# Revit family: 1SE_Trez_TC_2C_T_2500_With_Ramp
name_source: partatom
category: Specialty Equipment
units: mm (PartAtom-declared; Revit-internal decimal feet)

## family parameters
Always vertical = Yes
Cut with Voids When Loaded = Yes
Part Type = Normal
Room Calculation Point = No
Round Connector Dimension = Use Diameter
Shared = No
Work Plane-Based = No

## types (1)
- Platform-2300x2300mm with Door Height 2500mm
    Cabin = Speciality_Equipment_Trez_Cabin : Cabin
    Cabin or Platform = Speciality_Equipment_Trez_Platform : Platform
    Cabin or Platform Back = Yes
    Clear Depth = 2300 mm
    Clear Width = 2300 mm
    Clearance = 475 mm  [stored 1.5584 ft]
    Description = Trez Compact 2 Cylinders Tower. Goods only lift.
    Door Clear Height = 2500 mm  [stored 8.2021 ft]
    Door Clear Width = 2300 mm
    Headroom = 3100 mm
    Manufacturer = TREZ Ltd.
    Model = TC 2C T 2500
    Platform = Speciality_Equipment_Trez_Platform : Platform
    Platform Material = TREZ_Steel_Platform
    Profiles Material = TREZ_Steel_Profiles
    Rail Height = 7600 mm  [stored 24.9344 ft]
    Ramp Height = 250 mm  [stored 0.82021 ft]
    Ramp Material = TREZ_Steel_Platform
    Ramp Width = 3000 mm  [stored 9.84252 ft]
    Real Depth = 2300 mm
    Real Width = 2300 mm
    Safe Space = 600 mm
    Safe Working Load = 2500.00 kg
    Tower Cladding Material = TREZ_Steel_Cladding
    Tower Depth = 2480 mm
    Tower Width = 3250 mm
    Travel = 4500 mm
    URL = https://trez.bg

note: [stored X ft] marks values corroborated as IEEE doubles in the binary element streams (Revit-internal decimal feet)

## geometry (parser evidence)
native form markers: Sweep x13
no freeform markers — native parametric forms only
